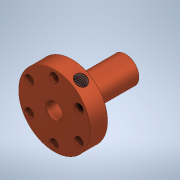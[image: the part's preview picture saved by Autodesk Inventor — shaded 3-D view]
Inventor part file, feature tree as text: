
AUTODESK INVENTOR PART (.ipt)
format: ipt  version: 2020 (Build 240168000, 168)  size: 167,424 bytes
history: native  units: mm
features: sketch x3, hole x2, plane x2, revolve x1, pattern_circular x1, chamfer x1
ambient origin geometry x8: Origin, YZ Plane, XZ Plane, XY Plane, X Axis, Y Axis, Z Axis, Center Point
bodies: Solid1 (feature_tree)
feature tree (10):
  revolve  "Revolution1"  [1 undecoded]
  hole  "Hole1"  [1 undecoded]
  pattern_circular  "Circular Pattern1"  Count=4  [1 undecoded]
  plane  "Work Plane2"
  hole  "Hole2"  [1 undecoded]
  chamfer  "Chamfer1"  Distance=60.0mm Angle=360.0deg
  sketch  "Sketch1"  dims[d0=9.0mm d1=15.0mm]
  sketch  "Sketch2"  dims[d2=30.0mm d3=10.0mm d4=40.0mm]
  plane  "Work Plane1"
  sketch  "Sketch3"  dims[d5=90.0deg d6=16.0mm d7=5.0mm d8=6.0mm d9=4.0mm d10=2.0mm d11=90.0deg d12=8.0mm d13=20.594885mm d14=60.0mm d15=360.0deg d17=60.0deg d18=6.647mm d19=10.0mm d20=4.0mm d21=2.0mm d22=90.0deg d23=20.2mm d24=20.594885mm d25=0.2mm d26=2.0mm d27=45.0deg]
note: 4 required parameter values undecoded (feature->parameter linkage not recoverable at this tier; creation-order binding heuristic only, values carry confidence <= 0.55)